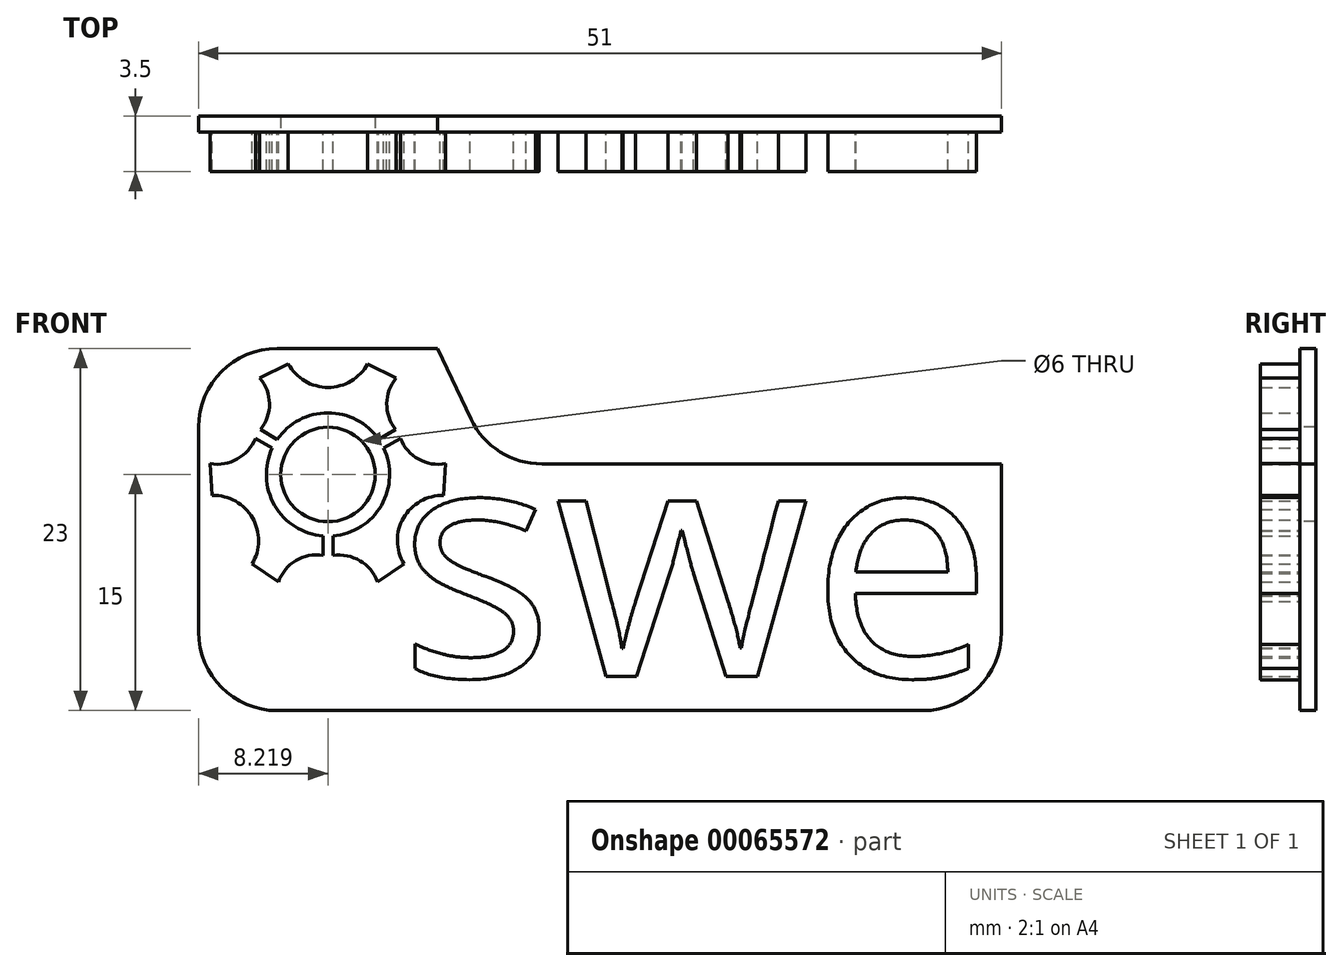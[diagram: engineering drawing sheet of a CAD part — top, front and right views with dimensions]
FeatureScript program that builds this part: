
annotation { "Feature Type Name" : "Feature", "Feature Type Description" : "" }
export const myFeature = defineFeature(function(context is Context, id is Id, definition is map)
    precondition{}
    {
        {
            var Q0;
            Q0=qCreatedBy(makeId("Front.planeOp"),FACE);
            var sketch = newSketch(context, id + "F0", { "sketchPlane" : qUnion([Q0])});
            skLineSegment(sketch, "E0.bottom", {"start": v(-23, 10) * mm, "end": v(28, 10) * mm});
            skLineSegment(sketch, "E0.top", {"start": v(-23, -13) * mm, "end": v(28, -13) * mm});
            skLineSegment(sketch, "E0.left", {"start": v(-23, 10) * mm, "end": v(-23, -13) * mm});
            skLineSegment(sketch, "E0.right", {"start": v(28, 10) * mm, "end": v(28, -13) * mm});
            skSolve(sketch);
        }
        {
            var Q0;
            Q0=makeQuery(id+"F0.imprint","IMPRINT",FACE,{"disambiguationData":[TD([[makeQuery(id+"F0.imprint","IMPRINT",EDGE,{"derivedFrom":sQuery(id+"F0.wireOp",EDGE,"E0.bottom")}),-1.0]])]});
            extrude(context, id + "F1", {"entities" : qUnion([Q0]), "oppositeDirection" : true, "depth" : 1 * mm});
        }
        {
            var Q0;
            Q0=makeQuery(id+"F1.opExtrude","CAP_FACE",FACE,{"disambiguationData":[OSD([sQuery(id+"F0.wireOp",EDGE,"E0.bottom"),sQuery(id+"F0.wireOp",EDGE,"E0.top"),sQuery(id+"F0.wireOp",EDGE,"E0.left"),sQuery(id+"F0.wireOp",EDGE,"E0.right")])],"isStart":true});
            var sketch = newSketch(context, id + "F2", { "sketchPlane" : qUnion([Q0])});
            skText(sketch, "E1", { "text": "swe", "fontName": "OpenSans-Regular.ttf"});
            const initialGuessF2  = {"E1": [-0.01035, -0.01083, 1, 0, 0.015]};
            skSetInitialGuess(sketch, initialGuessF2);
            skSolve(sketch);
        }
        {
            var Q0;
            Q0=qSketchRegion(id+"F2",true);
            extrude(context, id + "F3", {"entities" : qUnion([Q0]), "operationType" : NewBodyOperationType.ADD, "depth" : 2.5 * mm});
        }
        {
            var Q0;
            Q0=makeQuery(id+"F1.opExtrude","CAP_FACE",FACE,{"disambiguationData":[OSD([sQuery(id+"F0.wireOp",EDGE,"E0.bottom"),sQuery(id+"F0.wireOp",EDGE,"E0.top"),sQuery(id+"F0.wireOp",EDGE,"E0.left"),sQuery(id+"F0.wireOp",EDGE,"E0.right")])],"isStart":true});
            var sketch = newSketch(context, id + "F4", { "sketchPlane" : qUnion([Q0])});
            skCircle(sketch, "E2", {"center": v(-14.78, 2) * mm, "radius": 3 * mm});
            skSolve(sketch);
        }
        {
            var Q0;
            Q0=qSketchRegion(id+"F4",true);
            var Q1;
            Q1=makeQuery(id+"F1.opExtrude","CAP_FACE",FACE,{"disambiguationData":[OSD([sQuery(id+"F0.wireOp",EDGE,"E0.bottom"),sQuery(id+"F0.wireOp",EDGE,"E0.top"),sQuery(id+"F0.wireOp",EDGE,"E0.left"),sQuery(id+"F0.wireOp",EDGE,"E0.right")])],"isStart":false});
            extrude(context, id + "F5", {"entities" : qUnion([Q0]), "operationType" : NewBodyOperationType.REMOVE, "endBound" : BoundingType.UP_TO_SURFACE, "oppositeDirection" : true, "endBoundEntityFace" : qUnion([Q1]), "depth" : 25 * mm});
        }
        {
            var Q0;
            Q0=makeQuery(id+"F1.opExtrude","SWEPT_EDGE",EDGE,{"disambiguationData":[OSD([sQuery(id+"F0.wireOp",EDGE,"E0.bottom"),sQuery(id+"F0.wireOp",EDGE,"E0.left")])]});
            var Q1;
            Q1=makeQuery(id+"F1.opExtrude","SWEPT_EDGE",EDGE,{"disambiguationData":[OSD([sQuery(id+"F0.wireOp",EDGE,"E0.top"),sQuery(id+"F0.wireOp",EDGE,"E0.right")])]});
            var Q2;
            Q2=makeQuery(id+"F1.opExtrude","SWEPT_EDGE",EDGE,{"disambiguationData":[OSD([sQuery(id+"F0.wireOp",EDGE,"E0.bottom"),sQuery(id+"F0.wireOp",EDGE,"E0.right")])]});
            var Q3;
            Q3=makeQuery(id+"F1.opExtrude","SWEPT_EDGE",EDGE,{"disambiguationData":[OSD([sQuery(id+"F0.wireOp",EDGE,"E0.top"),sQuery(id+"F0.wireOp",EDGE,"E0.left")])]});
            fillet(context, id + "F6", {"entities" : qUnion([Q0, Q1, Q2, Q3]), "radius" : 5 * mm, "tangentPropagation" : true, "allowEdgeOverflow" : false});
        }
        {
            var Q0;
            {var subQ0=sQuery(id+"F0.wireOp",EDGE,"E0.top");var subQ1=sQuery(id+"F0.wireOp",EDGE,"E0.right");var subQ2=sQuery(id+"F0.wireOp",EDGE,"E0.bottom");var subQ3=sQuery(id+"F0.wireOp",EDGE,"E0.left");Q0=makeQuery(id+"F3.boolean.opBoolean","SPLIT",FACE,{"disambiguationData":[TD([makeQuery(id+"F1.opExtrude","SWEPT_FACE",FACE,{"disambiguationData":[OSD([subQ2])]})])],"derivedFrom":makeQuery(id+"F1.opExtrude","CAP_FACE",FACE,{"disambiguationData":[OSD([subQ2,subQ0,subQ3,subQ1])],"isStart":true})});}
            var sketch = newSketch(context, id + "F7", { "sketchPlane" : qUnion([Q0])});
            skPoint(sketch, "E3.centerSnap0", {"position": v(-14.78, 6.88) * mm});
            skLineSegment(sketch, "E4", {"start": v(-14.78, 13.75) * mm, "end": v(-14.78, 2) * mm, "construction": true});
            skLineSegment(sketch, "E5", {"start": v(-17.3, 9.03) * mm, "end": v(-12.26, 9.03) * mm, "construction": true});
            skLineSegment(sketch, "E6", {"start": v(-17.3, 9.03) * mm, "end": v(-19.11, 8.13) * mm, "construction": true});
            skArc(sketch, "E7", {"start": v(-17.3, 9.03) * mm, "mid": v(-14.78, 7.38) * mm, "end": v(-12.26, 9.03) * mm, "construction": true});
            skLineSegment(sketch, "E8", {"start": v(-12.26, 9.03) * mm, "end": v(-10.45, 8.13) * mm, "construction": true});
            skLineSegment(sketch, "E9", {"start": v(-10.45, 8.13) * mm, "end": v(-10.83, 6.63) * mm, "construction": true});
            skArc(sketch, "E10", {"start": v(-10.83, 6.63) * mm, "mid": v(-10.9, 5.69) * mm, "end": v(-10.5, 4.85) * mm, "construction": true});
            skLineSegment(sketch, "E11", {"start": v(-10.5, 4.85) * mm, "end": v(-11.56, 4.23) * mm, "construction": true});
            skArc(sketch, "E12", {"start": v(-11.56, 4.23) * mm, "mid": v(-14.78, 5.92) * mm, "end": v(-18, 4.23) * mm, "construction": true});
            skLineSegment(sketch, "E13", {"start": v(-19.07, 4.85) * mm, "end": v(-18, 4.23) * mm, "construction": true});
            skArc(sketch, "E14", {"start": v(-19.07, 4.85) * mm, "mid": v(-18.66, 5.69) * mm, "end": v(-18.73, 6.63) * mm, "construction": true});
            skLineSegment(sketch, "E15", {"start": v(-19.11, 8.13) * mm, "end": v(-18.73, 6.63) * mm, "construction": true});
            skLineSegment(sketch, "E16", {"start": v(-18, 4.23) * mm, "end": v(-11.56, 4.23) * mm, "construction": true});
            skLineSegment(sketch, "E17", {"start": v(-18.73, 6.63) * mm, "end": v(-10.83, 6.63) * mm, "construction": true});
            skLineSegment(sketch, "E18", {"start": v(-10.45, 8.13) * mm, "end": v(-19.11, 8.13) * mm, "construction": true});
            skLineSegment(sketch, "E19", {"start": v(-19.11, 8.13) * mm, "end": v(-17.3, 9.03) * mm});
            skLineSegment(sketch, "E20", {"start": v(-12.26, 9.03) * mm, "end": v(-10.45, 8.13) * mm});
            skLineSegment(sketch, "E21", {"start": v(-10.5, 4.85) * mm, "end": v(-11.56, 4.23) * mm});
            skLineSegment(sketch, "E22", {"start": v(-18, 4.23) * mm, "end": v(-19.07, 4.85) * mm});
            skArc(sketch, "E23", {"start": v(-17.3, 9.03) * mm, "mid": v(-14.78, 7.53) * mm, "end": v(-12.26, 9.03) * mm});
            skArc(sketch, "E24", {"start": v(-11.56, 4.23) * mm, "mid": v(-14.78, 5.92) * mm, "end": v(-18, 4.23) * mm});
            skArc(sketch, "E25", {"start": v(-10.45, 8.13) * mm, "mid": v(-11.05, 6.5) * mm, "end": v(-10.5, 4.85) * mm});
            skArc(sketch, "E26", {"start": v(-19.07, 4.85) * mm, "mid": v(-18.5, 6.5) * mm, "end": v(-19.11, 8.13) * mm});
            skArc(sketch, "E27.1.0", {"start": v(-19.6, -3.7) * mm, "mid": v(-19.57, -0.77) * mm, "end": v(-22.13, 0.67) * mm});
            skLineSegment(sketch, "E27.1.1", {"start": v(-17.93, -4.82) * mm, "end": v(-19.6, -3.7) * mm});
            skArc(sketch, "E27.1.2", {"start": v(-15.1, -3.14) * mm, "mid": v(-16.82, -3.47) * mm, "end": v(-17.93, -4.82) * mm});
            skLineSegment(sketch, "E27.1.3", {"start": v(-15.1, -1.9) * mm, "end": v(-15.1, -3.14) * mm});
            skArc(sketch, "E27.1.4", {"start": v(-18.32, 3.67) * mm, "mid": v(-18.17, 0.04) * mm, "end": v(-15.1, -1.9) * mm});
            skLineSegment(sketch, "E27.1.5", {"start": v(-19.4, 4.3) * mm, "end": v(-18.32, 3.67) * mm});
            skArc(sketch, "E27.1.6", {"start": v(-22.26, 2.69) * mm, "mid": v(-20.54, 2.98) * mm, "end": v(-19.4, 4.3) * mm});
            skLineSegment(sketch, "E27.1.7", {"start": v(-22.13, 0.67) * mm, "end": v(-22.26, 2.69) * mm});
            skArc(sketch, "E27.2.0", {"start": v(-7.44, 0.67) * mm, "mid": v(-10, -0.77) * mm, "end": v(-9.95, -3.7) * mm});
            skLineSegment(sketch, "E27.2.1", {"start": v(-7.3, 2.69) * mm, "end": v(-7.44, 0.67) * mm});
            skArc(sketch, "E27.2.2", {"start": v(-10.17, 4.3) * mm, "mid": v(-9.03, 2.97) * mm, "end": v(-7.3, 2.69) * mm});
            skLineSegment(sketch, "E27.2.3", {"start": v(-11.24, 3.67) * mm, "end": v(-10.17, 4.3) * mm});
            skArc(sketch, "E27.2.4", {"start": v(-14.46, -1.9) * mm, "mid": v(-11.4, 0.04) * mm, "end": v(-11.24, 3.67) * mm});
            skLineSegment(sketch, "E27.2.5", {"start": v(-14.46, -3.14) * mm, "end": v(-14.46, -1.9) * mm});
            skArc(sketch, "E27.2.6", {"start": v(-11.64, -4.82) * mm, "mid": v(-12.75, -3.48) * mm, "end": v(-14.46, -3.14) * mm});
            skLineSegment(sketch, "E27.2.7", {"start": v(-9.95, -3.7) * mm, "end": v(-11.64, -4.82) * mm});
            skLineSegment(sketch, "E28", {"start": v(-14.78, 2) * mm, "end": v(-19.07, 4.85) * mm, "construction": true});
            skLineSegment(sketch, "E29", {"start": v(-14.78, 2) * mm, "end": v(-10.5, 4.85) * mm, "construction": true});
            skLineSegment(sketch, "E30", {"start": v(-14.78, 2) * mm, "end": v(-17.3, 9.03) * mm, "construction": true});
            skLineSegment(sketch, "E31", {"start": v(-14.78, 2) * mm, "end": v(-12.26, 9.03) * mm, "construction": true});
            skLineSegment(sketch, "E32", {"start": v(-14.78, 2) * mm, "end": v(-10.45, 8.13) * mm, "construction": true});
            skLineSegment(sketch, "E33", {"start": v(-14.78, 2) * mm, "end": v(-19.11, 8.13) * mm, "construction": true});
            skLineSegment(sketch, "E34", {"start": v(-14.78, 2) * mm, "end": v(2.33, 2) * mm, "construction": true});
            skSolve(sketch);
        }
        {
            var Q0;
            Q0=qSketchRegion(id+"F7",true);
            extrude(context, id + "F8", {"entities" : qUnion([Q0]), "operationType" : NewBodyOperationType.ADD, "depth" : 2.5 * mm});
        }
        {
            var Q0;
            {var subQ0=sQuery(id+"F0.wireOp",EDGE,"E0.top");var subQ1=sQuery(id+"F0.wireOp",EDGE,"E0.right");var subQ2=sQuery(id+"F0.wireOp",EDGE,"E0.bottom");var subQ3=sQuery(id+"F0.wireOp",EDGE,"E0.left");Q0=makeQuery(id+"F3.boolean.opBoolean","SPLIT",FACE,{"disambiguationData":[TD([makeQuery(id+"F1.opExtrude","SWEPT_FACE",FACE,{"disambiguationData":[OSD([subQ2])]})])],"derivedFrom":makeQuery(id+"F1.opExtrude","CAP_FACE",FACE,{"disambiguationData":[OSD([subQ2,subQ0,subQ3,subQ1])],"isStart":true})});}
            var sketch = newSketch(context, id + "F9", { "sketchPlane" : qUnion([Q0])});
            skLineSegment(sketch, "E35", {"start": v(-7.83, 10) * mm, "end": v(-4.35, 2.67) * mm});
            skLineSegment(sketch, "E36", {"start": v(-4.35, 2.67) * mm, "end": v(28, 2.67) * mm});
            skLineSegment(sketch, "E37", {"start": v(28, 2.67) * mm, "end": v(28, 5) * mm});
            skLineSegment(sketch, "E38", {"start": v(-7.83, 10) * mm, "end": v(23, 10) * mm});
            skArc(sketch, "E39", {"start": v(28, 5) * mm, "mid": v(26.54, 8.54) * mm, "end": v(23, 10) * mm});
            skSolve(sketch);
        }
        {
            var Q0;
            Q0 = qSketchRegion(id + "F9", true);
            var Q1;
            Q1=makeQuery(id+"F1.opExtrude","CAP_FACE",FACE,{"disambiguationData":[OSD([sQuery(id+"F0.wireOp",EDGE,"E0.bottom"),sQuery(id+"F0.wireOp",EDGE,"E0.top"),sQuery(id+"F0.wireOp",EDGE,"E0.left"),sQuery(id+"F0.wireOp",EDGE,"E0.right")])],"isStart":false});
            extrude(context, id + "F10", {"entities" : qUnion([Q0]), "operationType" : NewBodyOperationType.REMOVE, "endBound" : BoundingType.UP_TO_SURFACE, "oppositeDirection" : true, "endBoundEntityFace" : qUnion([Q1]), "depth" : 25 * mm});
        }
        {
            var Q0;
            Q0=makeQuery(id+"F10.boolean.opBoolean","COPY",EDGE,{"derivedFrom":makeQuery(id+"F10.opExtrude","SWEPT_EDGE",EDGE,{"disambiguationData":[OSD([sQuery(id+"F0.wireOp",EDGE,"E0.bottom"),sQuery(id+"F9.wireOp",EDGE,"E35"),sQuery(id+"F9.wireOp",EDGE,"E38")])]})});
            var Q1;
            Q1=makeQuery(id+"F10.boolean.opBoolean","COPY",EDGE,{"derivedFrom":makeQuery(id+"F10.opExtrude","SWEPT_EDGE",EDGE,{"disambiguationData":[OSD([sQuery(id+"F9.wireOp",EDGE,"E35"),sQuery(id+"F9.wireOp",EDGE,"E36")])]})});
            var Q2;
            Q2=makeQuery(id+"F10.boolean.opBoolean","COPY",EDGE,{"derivedFrom":makeQuery(id+"F10.opExtrude","SWEPT_EDGE",EDGE,{"disambiguationData":[OSD([sQuery(id+"F0.wireOp",EDGE,"E0.right"),sQuery(id+"F9.wireOp",EDGE,"E36"),sQuery(id+"F9.wireOp",EDGE,"E37")])]})});
            fillet(context, id + "F11", {"entities" : qUnion([Q0, Q1, Q2]), "radius" : 5 * mm, "tangentPropagation" : true, "allowEdgeOverflow" : false});
        }
    });
